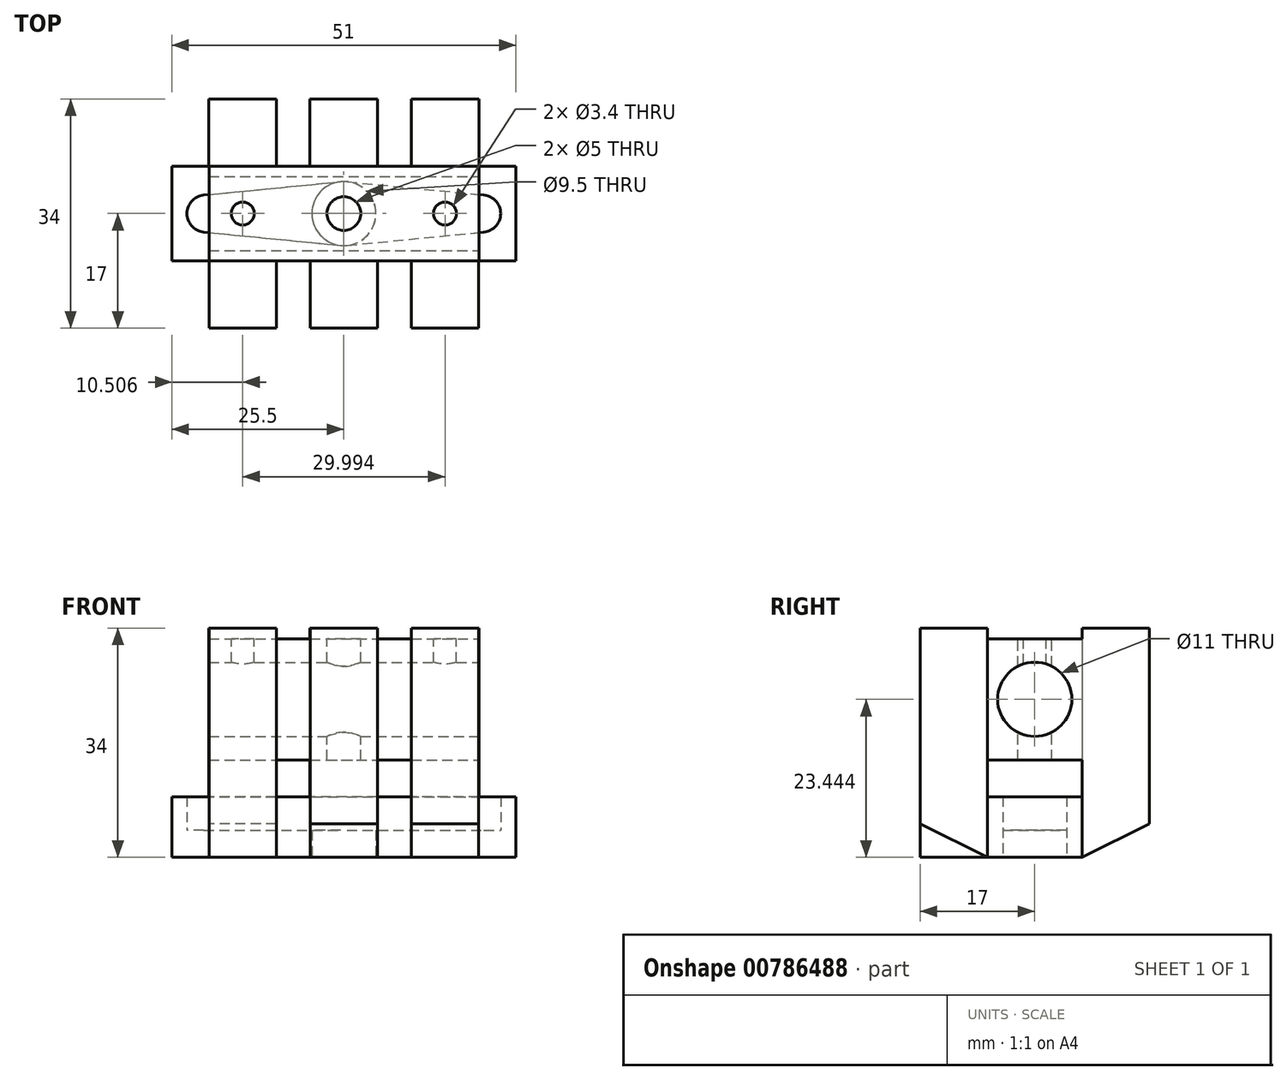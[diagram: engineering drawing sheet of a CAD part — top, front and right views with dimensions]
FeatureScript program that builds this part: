
annotation { "Feature Type Name" : "Feature", "Feature Type Description" : "" }
export const myFeature = defineFeature(function(context is Context, id is Id, definition is map)
    precondition{}
    {
        {
            var Q0;
            Q0=qCreatedBy(makeId("Top.planeOp"),FACE);
            var sketch = newSketch(context, id + "F0", { "sketchPlane" : qUnion([Q0])});
            skLineSegment(sketch, "E0.bottom", {"start": v(-25.5, 7) * mm, "end": v(25.5, 7) * mm});
            skLineSegment(sketch, "E0.top", {"start": v(-25.5, -7) * mm, "end": v(25.5, -7) * mm});
            skLineSegment(sketch, "E0.left", {"start": v(-25.5, 7) * mm, "end": v(-25.5, -7) * mm});
            skLineSegment(sketch, "E0.right", {"start": v(25.5, 7) * mm, "end": v(25.5, -7) * mm});
            skSolve(sketch);
        }
        {
            var Q0;
            Q0 = qSketchRegion(id + "F0", true);
            extrude(context, id + "F1", {"entities" : qUnion([Q0]), "depth" : 6 * mm, "offsetDistance" : 25 * mm});
        }
        {
            var Q0;
            Q0=makeQuery(id+"F1.opExtrude","CAP_FACE",FACE,{"disambiguationData":[OSD([sQuery(id+"F0.wireOp",EDGE,"E0.bottom"),sQuery(id+"F0.wireOp",EDGE,"E0.top"),sQuery(id+"F0.wireOp",EDGE,"E0.left"),sQuery(id+"F0.wireOp",EDGE,"E0.right")])],"isStart":true});
            var sketch = newSketch(context, id + "F2", { "sketchPlane" : qUnion([Q0])});
            skCircle(sketch, "E1", {"center": v(-20.5, 0) * mm, "radius": 2.75 * mm});
            skCircle(sketch, "E2", {"center": v(20.5, 0) * mm, "radius": 2.75 * mm});
            skCircle(sketch, "E3", {"center": v(0, 0) * mm, "radius": 4.75 * mm});
            skCircle(sketch, "E4", {"center": v(0, 0) * mm, "radius": 2.5 * mm});
            skLineSegment(sketch, "E5", {"start": v(-20.77, 2.74) * mm, "end": v(0, 4.77) * mm});
            skLineSegment(sketch, "E6", {"start": v(0.46, 4.73) * mm, "end": v(20.77, 2.74) * mm});
            skLineSegment(sketch, "E7", {"start": v(0.46, -4.73) * mm, "end": v(20.77, -2.74) * mm});
            skLineSegment(sketch, "E8", {"start": v(-20.77, -2.74) * mm, "end": v(-0.46, -4.73) * mm});
            skSolve(sketch);
        }
        {
            var Q0;
            Q0=makeQuery(id+"F2.imprint","IMPRINT",FACE,{"disambiguationData":[TD([[makeQuery(id+"F2.imprint","IMPRINT",EDGE,{"derivedFrom":sQuery(id+"F2.wireOp",EDGE,"E4")}),-1.0]])]});
            var Q1;
            Q1=makeQuery(id+"F2.imprint","IMPRINT",FACE,{"disambiguationData":[TD([[makeQuery(id+"F2.imprint","IMPRINT",EDGE,{"derivedFrom":sQuery(id+"F2.wireOp",EDGE,"E4")}),1.0]])]});
            extrude(context, id + "F3", {"entities" : qUnion([Q0, Q1]), "operationType" : NewBodyOperationType.REMOVE, "oppositeDirection" : true, "depth" : 4 * mm, "offsetDistance" : 25 * mm});
        }
        {
            var Q0;
            Q0=makeQuery(id+"F1.opExtrude","CAP_FACE",FACE,{"disambiguationData":[OSD([sQuery(id+"F0.wireOp",EDGE,"E0.bottom"),sQuery(id+"F0.wireOp",EDGE,"E0.top"),sQuery(id+"F0.wireOp",EDGE,"E0.left"),sQuery(id+"F0.wireOp",EDGE,"E0.right")])],"isStart":true});
            cPlane(context, id + "F4", {"entities" : qUnion([Q0]), "cplaneType" : CPlaneType.OFFSET, "offset" : 4 * mm, "oppositeDirection" : true, "width" : 150 * mm, "height" : 150 * mm});
        }
        {
            var Q0;
            Q0=qCreatedBy(id+"F4.planeOp",FACE);
            var sketch = newSketch(context, id + "F5", { "sketchPlane" : qUnion([Q0])});
            skArc(sketch, "E9", {"start": v(-20.77, 2.74) * mm, "mid": v(-23.25, 0) * mm, "end": v(-20.77, -2.74) * mm});
            skArc(sketch, "E10", {"start": v(20.77, -2.74) * mm, "mid": v(23.25, 0) * mm, "end": v(20.77, 2.74) * mm});
            skCircle(sketch, "E11", {"center": v(0, 0) * mm, "radius": 4.75 * mm});
            skLineSegment(sketch, "E12", {"start": v(-20.77, -2.74) * mm, "end": v(-0.46, -4.73) * mm});
            skLineSegment(sketch, "E13", {"start": v(0.46, 4.73) * mm, "end": v(20.77, 2.74) * mm});
            skLineSegment(sketch, "E14", {"start": v(0.46, -4.73) * mm, "end": v(20.77, -2.74) * mm});
            skLineSegment(sketch, "E15", {"start": v(-20.77, 2.74) * mm, "end": v(-0.46, 4.73) * mm});
            skSolve(sketch);
        }
        {
            var Q0;
            Q0 = qSketchRegion(id + "F5", true);
            extrude(context, id + "F6", {"entities" : qUnion([Q0]), "operationType" : NewBodyOperationType.REMOVE, "oppositeDirection" : true, "depth" : 2 * mm, "offsetDistance" : 25 * mm});
        }
        {
            var Q0;
            Q0=makeQuery(id+"F1.opExtrude","CAP_FACE",FACE,{"disambiguationData":[OSD([sQuery(id+"F0.wireOp",EDGE,"E0.bottom"),sQuery(id+"F0.wireOp",EDGE,"E0.top"),sQuery(id+"F0.wireOp",EDGE,"E0.left"),sQuery(id+"F0.wireOp",EDGE,"E0.right")])],"isStart":false});
            extrude(context, id + "F7", {"entities" : qUnion([Q0]), "operationType" : NewBodyOperationType.ADD, "depth" : 3 * mm, "offsetDistance" : 25 * mm});
        }
        {
            var Q0;
            {var subQ0=sQuery(id+"F0.wireOp",EDGE,"E0.top");Q0=makeQuery(id+"F7.boolean.opBoolean","MERGE",FACE,{"derivedFrom":[makeQuery(id+"F1.opExtrude","SWEPT_FACE",FACE,{"disambiguationData":[OSD([subQ0])]}),makeQuery(id+"F7.opExtrude","SWEPT_FACE",FACE,{"disambiguationData":[OSD([subQ0])]})]});}
            var sketch = newSketch(context, id + "F8", { "sketchPlane" : qUnion([Q0])});
            skLineSegment(sketch, "E16.bottom", {"start": v(20, 0) * mm, "end": v(10, 0) * mm});
            skLineSegment(sketch, "E16.top", {"start": v(20, 9) * mm, "end": v(10, 9) * mm});
            skLineSegment(sketch, "E16.left", {"start": v(20, 0) * mm, "end": v(20, 9) * mm});
            skLineSegment(sketch, "E16.right", {"start": v(10, 0) * mm, "end": v(10, 9) * mm});
            skLineSegment(sketch, "E17.bottom", {"start": v(5, 0) * mm, "end": v(-5, 0) * mm});
            skLineSegment(sketch, "E17.top", {"start": v(5, 9) * mm, "end": v(-5, 9) * mm});
            skLineSegment(sketch, "E17.left", {"start": v(5, 0) * mm, "end": v(5, 9) * mm});
            skLineSegment(sketch, "E17.right", {"start": v(-5, 0) * mm, "end": v(-5, 9) * mm});
            skLineSegment(sketch, "E18.bottom", {"start": v(-10, 0) * mm, "end": v(-20, 0) * mm});
            skLineSegment(sketch, "E18.top", {"start": v(-10, 9) * mm, "end": v(-20, 9) * mm});
            skLineSegment(sketch, "E18.left", {"start": v(-10, 0) * mm, "end": v(-10, 9) * mm});
            skLineSegment(sketch, "E18.right", {"start": v(-20, 0) * mm, "end": v(-20, 9) * mm});
            skLineSegment(sketch, "E19", {"start": v(0, 0) * mm, "end": v(-25.5, 0) * mm});
            skSolve(sketch);
        }
        {
            var Q0;
            Q0 = qSketchRegion(id + "F8", true);
            extrude(context, id + "F9", {"entities" : qUnion([Q0]), "operationType" : NewBodyOperationType.ADD, "depth" : 10 * mm, "offsetDistance" : 25 * mm});
        }
        {
            var Q0;
            Q0=makeQuery(id+"F9.boolean.opBoolean","MERGE",FACE,{"derivedFrom":[makeQuery(id+"F7.opExtrude","CAP_FACE",FACE,{"disambiguationData":[OSD([sQuery(id+"F0.wireOp",EDGE,"E0.bottom"),sQuery(id+"F0.wireOp",EDGE,"E0.top"),sQuery(id+"F0.wireOp",EDGE,"E0.left"),sQuery(id+"F0.wireOp",EDGE,"E0.right")])],"isStart":false}),makeQuery(id+"F9.opExtrude","SWEPT_FACE",FACE,{"disambiguationData":[OSD([sQuery(id+"F8.wireOp",EDGE,"E16.top")])]}),makeQuery(id+"F9.opExtrude","SWEPT_FACE",FACE,{"disambiguationData":[OSD([sQuery(id+"F8.wireOp",EDGE,"E17.top")])]}),makeQuery(id+"F9.opExtrude","SWEPT_FACE",FACE,{"disambiguationData":[OSD([sQuery(id+"F8.wireOp",EDGE,"E18.top")])]})]});
            var sketch = newSketch(context, id + "F10", { "sketchPlane" : qUnion([Q0])});
            skLineSegment(sketch, "E20.bottom", {"start": v(20, -17) * mm, "end": v(10, -17) * mm});
            skLineSegment(sketch, "E20.top", {"start": v(20, -7) * mm, "end": v(10, -7) * mm});
            skLineSegment(sketch, "E20.left", {"start": v(20, -17) * mm, "end": v(20, -7) * mm});
            skLineSegment(sketch, "E20.right", {"start": v(10, -17) * mm, "end": v(10, -7) * mm});
            skLineSegment(sketch, "E21.bottom", {"start": v(5, -17) * mm, "end": v(-5, -17) * mm});
            skLineSegment(sketch, "E21.top", {"start": v(5, -7) * mm, "end": v(-5, -7) * mm});
            skLineSegment(sketch, "E21.left", {"start": v(5, -17) * mm, "end": v(5, -7) * mm});
            skLineSegment(sketch, "E21.right", {"start": v(-5, -17) * mm, "end": v(-5, -7) * mm});
            skLineSegment(sketch, "E22.bottom", {"start": v(-10, -17) * mm, "end": v(-20, -17) * mm});
            skLineSegment(sketch, "E22.top", {"start": v(-10, -7) * mm, "end": v(-20, -7) * mm});
            skLineSegment(sketch, "E22.left", {"start": v(-10, -17) * mm, "end": v(-10, -7) * mm});
            skLineSegment(sketch, "E22.right", {"start": v(-20, -17) * mm, "end": v(-20, -7) * mm});
            skSolve(sketch);
        }
        {
            var Q0;
            Q0 = qSketchRegion(id + "F10", true);
            extrude(context, id + "F11", {"entities" : qUnion([Q0]), "operationType" : NewBodyOperationType.ADD, "depth" : 25 * mm, "offsetDistance" : 25 * mm});
        }
        {
            var Q0;
            {var subQ0=sQuery(id+"F0.wireOp",EDGE,"E0.bottom");Q0=makeQuery(id+"F7.boolean.opBoolean","MERGE",FACE,{"derivedFrom":[makeQuery(id+"F1.opExtrude","SWEPT_FACE",FACE,{"disambiguationData":[OSD([subQ0])]}),makeQuery(id+"F7.opExtrude","SWEPT_FACE",FACE,{"disambiguationData":[OSD([subQ0])]})]});}
            var sketch = newSketch(context, id + "F12", { "sketchPlane" : qUnion([Q0])});
            skLineSegment(sketch, "E23.bottom", {"start": v(-20.01, 9) * mm, "end": v(-10, 9) * mm});
            skLineSegment(sketch, "E23.top", {"start": v(-20.01, 0) * mm, "end": v(-10, 0) * mm});
            skLineSegment(sketch, "E23.left", {"start": v(-20.01, 9) * mm, "end": v(-20.01, 0) * mm});
            skLineSegment(sketch, "E23.right", {"start": v(-10, 9) * mm, "end": v(-10, 0) * mm});
            skLineSegment(sketch, "E24.bottom", {"start": v(-5, 9) * mm, "end": v(5.02, 9) * mm});
            skLineSegment(sketch, "E24.top", {"start": v(-5, 0) * mm, "end": v(5.02, 0) * mm});
            skLineSegment(sketch, "E24.left", {"start": v(-5, 9) * mm, "end": v(-5, 0) * mm});
            skLineSegment(sketch, "E24.right", {"start": v(5.02, 9) * mm, "end": v(5.02, 0) * mm});
            skLineSegment(sketch, "E25.bottom", {"start": v(10, 9) * mm, "end": v(20.02, 9) * mm});
            skLineSegment(sketch, "E25.top", {"start": v(10, 0) * mm, "end": v(20.02, 0) * mm});
            skLineSegment(sketch, "E25.left", {"start": v(10, 9) * mm, "end": v(10, 0) * mm});
            skLineSegment(sketch, "E25.right", {"start": v(20.02, 9) * mm, "end": v(20.02, 0) * mm});
            skSolve(sketch);
        }
        {
            var Q0;
            Q0 = qSketchRegion(id + "F12", true);
            extrude(context, id + "F13", {"entities" : qUnion([Q0]), "operationType" : NewBodyOperationType.ADD, "depth" : 10 * mm, "offsetDistance" : 25 * mm});
        }
        {
            var Q0;
            Q0=makeQuery(id+"F13.boolean.opBoolean","MERGE",FACE,{"derivedFrom":[makeQuery(id+"F9.boolean.opBoolean","MERGE",FACE,{"derivedFrom":[makeQuery(id+"F7.opExtrude","CAP_FACE",FACE,{"disambiguationData":[OSD([sQuery(id+"F0.wireOp",EDGE,"E0.bottom"),sQuery(id+"F0.wireOp",EDGE,"E0.top"),sQuery(id+"F0.wireOp",EDGE,"E0.left"),sQuery(id+"F0.wireOp",EDGE,"E0.right")])],"isStart":false}),makeQuery(id+"F9.opExtrude","SWEPT_FACE",FACE,{"disambiguationData":[OSD([sQuery(id+"F8.wireOp",EDGE,"E16.top")])]}),makeQuery(id+"F9.opExtrude","SWEPT_FACE",FACE,{"disambiguationData":[OSD([sQuery(id+"F8.wireOp",EDGE,"E17.top")])]}),makeQuery(id+"F9.opExtrude","SWEPT_FACE",FACE,{"disambiguationData":[OSD([sQuery(id+"F8.wireOp",EDGE,"E18.top")])]})]}),makeQuery(id+"F13.opExtrude","SWEPT_FACE",FACE,{"disambiguationData":[OSD([sQuery(id+"F12.wireOp",EDGE,"E23.bottom")])]}),makeQuery(id+"F13.opExtrude","SWEPT_FACE",FACE,{"disambiguationData":[OSD([sQuery(id+"F12.wireOp",EDGE,"E24.bottom")])]}),makeQuery(id+"F13.opExtrude","SWEPT_FACE",FACE,{"disambiguationData":[OSD([sQuery(id+"F12.wireOp",EDGE,"E25.bottom")])]})]});
            var sketch = newSketch(context, id + "F14", { "sketchPlane" : qUnion([Q0])});
            skLineSegment(sketch, "E26.bottom", {"start": v(20.01, 7) * mm, "end": v(10, 7) * mm});
            skLineSegment(sketch, "E26.top", {"start": v(20.01, 17) * mm, "end": v(10, 17) * mm});
            skLineSegment(sketch, "E26.left", {"start": v(20.01, 7) * mm, "end": v(20.01, 17) * mm});
            skLineSegment(sketch, "E26.right", {"start": v(10, 7) * mm, "end": v(10, 17) * mm});
            skLineSegment(sketch, "E27.bottom", {"start": v(5, 7) * mm, "end": v(-5.02, 7) * mm});
            skLineSegment(sketch, "E27.top", {"start": v(5, 17) * mm, "end": v(-5.02, 17) * mm});
            skLineSegment(sketch, "E27.left", {"start": v(5, 7) * mm, "end": v(5, 17) * mm});
            skLineSegment(sketch, "E27.right", {"start": v(-5.02, 7) * mm, "end": v(-5.02, 17) * mm});
            skLineSegment(sketch, "E28.bottom", {"start": v(-10, 7) * mm, "end": v(-20.02, 7) * mm});
            skLineSegment(sketch, "E28.top", {"start": v(-10, 17) * mm, "end": v(-20.02, 17) * mm});
            skLineSegment(sketch, "E28.left", {"start": v(-10, 7) * mm, "end": v(-10, 17) * mm});
            skLineSegment(sketch, "E28.right", {"start": v(-20.02, 7) * mm, "end": v(-20.02, 17) * mm});
            skSolve(sketch);
        }
        {
            var Q0;
            Q0 = qSketchRegion(id + "F14", true);
            extrude(context, id + "F15", {"entities" : qUnion([Q0]), "operationType" : NewBodyOperationType.ADD, "depth" : 25 * mm, "offsetDistance" : 25 * mm});
        }
        {
            var Q0;
            Q0=makeQuery(id+"F15.boolean.opBoolean","MERGE",FACE,{"derivedFrom":[makeQuery(id+"F13.opExtrude","SWEPT_FACE",FACE,{"disambiguationData":[OSD([sQuery(id+"F12.wireOp",EDGE,"E23.left")])]}),makeQuery(id+"F15.opExtrude","SWEPT_FACE",FACE,{"disambiguationData":[OSD([sQuery(id+"F14.wireOp",EDGE,"E26.left")])]})]});
            var sketch = newSketch(context, id + "F16", { "sketchPlane" : qUnion([Q0])});
            skLineSegment(sketch, "E29.bottom", {"start": v(-7, 14.43) * mm, "end": v(7, 14.43) * mm});
            skLineSegment(sketch, "E29.top", {"start": v(-7, 32.43) * mm, "end": v(7, 32.43) * mm});
            skLineSegment(sketch, "E29.left", {"start": v(-7, 14.43) * mm, "end": v(-7, 32.43) * mm});
            skLineSegment(sketch, "E29.right", {"start": v(7, 14.43) * mm, "end": v(7, 32.43) * mm});
            skCircle(sketch, "E30", {"center": v(0, 23.44) * mm, "radius": 5.5 * mm});
            skSolve(sketch);
        }
        {
            var Q0;
            Q0 = qSketchRegion(id + "F16", true);
            extrude(context, id + "F17", {"entities" : qUnion([Q0]), "operationType" : NewBodyOperationType.ADD, "oppositeDirection" : true, "depth" : 40 * mm, "offsetDistance" : 25 * mm});
        }
        {
            var Q0;
            Q0=makeQuery(id+"F17.opExtrude","SWEPT_FACE",FACE,{"disambiguationData":[OSD([sQuery(id+"F16.wireOp",EDGE,"E29.top")])]});
            var sketch = newSketch(context, id + "F18", { "sketchPlane" : qUnion([Q0])});
            skCircle(sketch, "E31", {"center": v(15, 0) * mm, "radius": 1.7 * mm});
            skPoint(sketch, "E31.centerSnap0", {"position": v(15, -7) * mm});
            skCircle(sketch, "E32", {"center": v(-15, 0) * mm, "radius": 1.7 * mm});
            skPoint(sketch, "E32.centerSnap0", {"position": v(-15, -7) * mm});
            skSolve(sketch);
        }
        {
            var Q0;
            Q0 = qSketchRegion(id + "F18", true);
            extrude(context, id + "F19", {"entities" : qUnion([Q0]), "operationType" : NewBodyOperationType.REMOVE, "oppositeDirection" : true, "depth" : 5 * mm, "offsetDistance" : 25 * mm});
        }
        {
            var Q0;
            Q0=makeQuery(id+"F17.opExtrude","SWEPT_FACE",FACE,{"disambiguationData":[OSD([sQuery(id+"F16.wireOp",EDGE,"E29.top")])]});
            var sketch = newSketch(context, id + "F20", { "sketchPlane" : qUnion([Q0])});
            skCircle(sketch, "E33", {"center": v(0, 0) * mm, "radius": 2.5 * mm});
            skSolve(sketch);
        }
        {
            var Q0;
            Q0 = qSketchRegion(id + "F20", true);
            extrude(context, id + "F21", {"entities" : qUnion([Q0]), "operationType" : NewBodyOperationType.REMOVE, "oppositeDirection" : true, "depth" : 20 * mm, "offsetDistance" : 25 * mm});
        }
        {
            var Q0;
            Q0=makeQuery(id+"F13.opExtrude","CAP_EDGE",EDGE,{"disambiguationData":[OSD([sQuery(id+"F12.wireOp",EDGE,"E23.top")])],"isStart":false});
            var Q1;
            Q1=makeQuery(id+"F13.opExtrude","CAP_EDGE",EDGE,{"disambiguationData":[OSD([sQuery(id+"F12.wireOp",EDGE,"E24.top")])],"isStart":false});
            var Q2;
            Q2=makeQuery(id+"F13.opExtrude","CAP_EDGE",EDGE,{"disambiguationData":[OSD([sQuery(id+"F12.wireOp",EDGE,"E25.top")])],"isStart":false});
            var Q3;
            Q3=makeQuery(id+"F9.opExtrude","CAP_EDGE",EDGE,{"disambiguationData":[OSD([sQuery(id+"F8.wireOp",EDGE,"E16.bottom")])],"isStart":false});
            var Q4;
            Q4=makeQuery(id+"F9.opExtrude","CAP_EDGE",EDGE,{"disambiguationData":[OSD([sQuery(id+"F8.wireOp",EDGE,"E17.bottom"),sQuery(id+"F8.wireOp",EDGE,"E19")])],"isStart":false});
            var Q5;
            Q5=makeQuery(id+"F9.opExtrude","CAP_EDGE",EDGE,{"disambiguationData":[OSD([sQuery(id+"F8.wireOp",EDGE,"E19")])],"isStart":false});
            chamfer(context, id + "F22", {"entities" : qUnion([Q0, Q1, Q2, Q3, Q4, Q5]), "chamferType" : ChamferType.TWO_OFFSETS, "width1" : 10 * mm, "oppositeDirection" : false, "width2" : 5 * mm, "tangentPropagation" : true});
        }
    });
